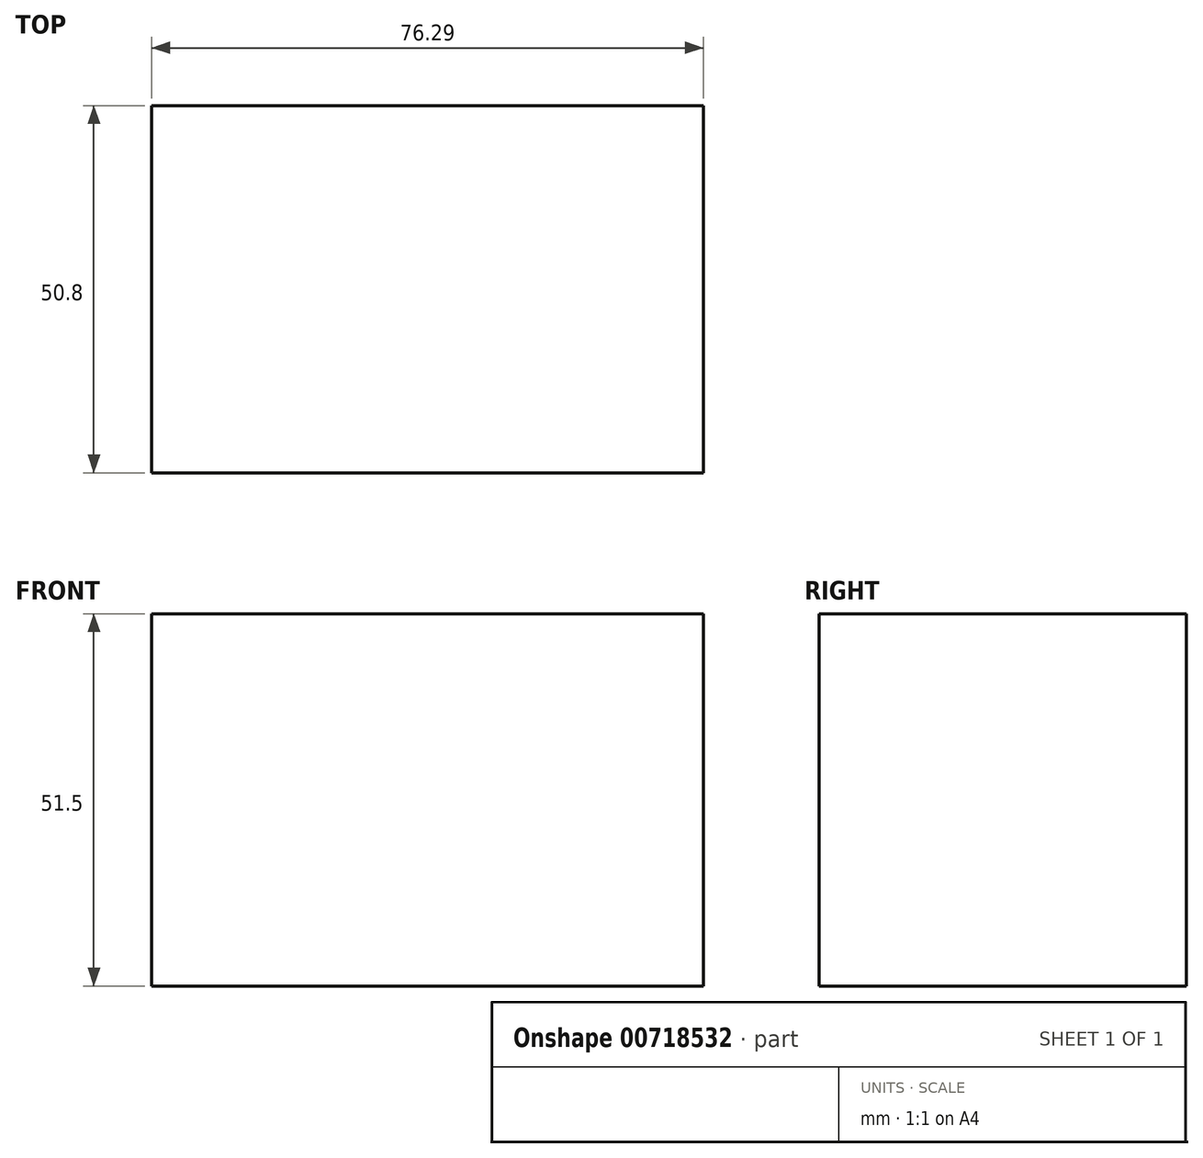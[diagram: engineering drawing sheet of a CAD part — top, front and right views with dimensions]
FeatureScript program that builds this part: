
annotation { "Feature Type Name" : "Feature", "Feature Type Description" : "" }
export const myFeature = defineFeature(function(context is Context, id is Id, definition is map)
    precondition{}
    {
        {
            var Q0;
            Q0=qCreatedBy(makeId("Front.planeOp"),FACE);
            var sketch = newSketch(context, id + "F0", { "sketchPlane" : qUnion([Q0])});
            skLineSegment(sketch, "E0.bottom", {"start": v(-40.89, 51.39) * mm, "end": v(-18, 51.39) * mm});
            skLineSegment(sketch, "E0.top", {"start": v(-40.89, 39.37) * mm, "end": v(-18, 39.37) * mm});
            skLineSegment(sketch, "E0.left", {"start": v(-40.89, 51.39) * mm, "end": v(-40.89, 39.37) * mm});
            skLineSegment(sketch, "E0.right", {"start": v(-18, 51.39) * mm, "end": v(-18, 39.37) * mm});
            skLineSegment(sketch, "E1.bottom", {"start": v(46.84, -12.13) * mm, "end": v(-29.45, -12.13) * mm});
            skLineSegment(sketch, "E1.top", {"start": v(46.84, 39.37) * mm, "end": v(-29.45, 39.37) * mm});
            skLineSegment(sketch, "E1.left", {"start": v(46.84, -12.13) * mm, "end": v(46.84, 39.37) * mm});
            skLineSegment(sketch, "E1.right", {"start": v(-29.45, -12.13) * mm, "end": v(-29.45, 39.37) * mm});
            skLineSegment(sketch, "E2.bottom", {"start": v(-40.89, 51.39) * mm, "end": v(-40.89, 51.39) * mm});
            skLineSegment(sketch, "E2.top", {"start": v(-40.89, 51.39) * mm, "end": v(-40.89, 51.39) * mm});
            skLineSegment(sketch, "E2.left", {"start": v(-40.89, 51.39) * mm, "end": v(-40.89, 51.39) * mm});
            skLineSegment(sketch, "E2.right", {"start": v(-40.89, 51.39) * mm, "end": v(-40.89, 51.39) * mm});
            skLineSegment(sketch, "E3.bottom", {"start": v(-40.89, 51.39) * mm, "end": v(-29.45, 51.39) * mm, "construction": true});
            skLineSegment(sketch, "E3.top", {"start": v(-40.89, 51.39) * mm, "end": v(-29.45, 51.39) * mm, "construction": true});
            skLineSegment(sketch, "E3.right", {"start": v(-29.45, 51.39) * mm, "end": v(-29.45, 51.39) * mm});
            skSolve(sketch);
        }
        {
            var Q0;
            Q0=makeQuery(id+"F0.imprint","IMPRINT",FACE,{"disambiguationData":[TD([[makeQuery(id+"F0.imprint","IMPRINT",EDGE,{"derivedFrom":sQuery(id+"F0.wireOp",EDGE,"E1.bottom")}),-1.0]])]});
            extrude(context, id + "F1", {"entities" : qUnion([Q0]), "depth" : 50.8 * mm, "offsetDistance" : 25.4 * mm});
        }
    });
